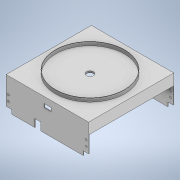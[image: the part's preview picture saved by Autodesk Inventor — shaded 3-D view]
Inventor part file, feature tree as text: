
AUTODESK INVENTOR PART (.ipt)
format: ipt  version: 2022 (Build 260153000, 153)  size: 213,504 bytes
history: native  units: in
note: dims shown in document units (in); Inventor stores cm internally (conversion verified against a paired STEP export)
features: extrude x9, sketch x6
ambient origin geometry x8: Origin, YZ Plane, XZ Plane, XY Plane, X Axis, Y Axis, Z Axis, Center Point
bodies: Solid1 (feature_tree)
feature tree (15):
  sketch  "Sketch2"  dims[d0=4.685in d1=1.5748in]
  sketch  "Sketch3"  dims[d2=0.315in d3=0.9449in]
  extrude  "Extrusion1"  Depth=1.5748in
  extrude  "Extrusion2"  Depth=0.315in
  extrude  "Extrusion3"  Depth=0.3031in
  sketch  "Sketch4"  dims[d4=0.1102in d5=0.3031in]
  extrude  "Extrusion4"  Depth=0.1102in
  extrude  "Extrusion5"  Depth=0.315in
  extrude  "Extrusion6"  Depth=0.6998in
  extrude  "Extrusion7"  Depth=0.6998in
  extrude  "Extrusion8"  Depth=0.6998in
  extrude  "Extrusion9"  Depth=0.6998in
  sketch  "Sketch5"  dims[d6=0.2053in d7=0.1102in]
  sketch  "Sketch6"  dims[d8=0.3346in d9=0.315in]
  sketch  "Sketch7"  dims[d10=0.9449in d12=0.1102in d13=0.3031in d15=0.1929in d16=0.1102in d17=0.3346in d18=0.4055in d19=0.1969in d20=1.0236in d21=4.6457in d22=4.8031in d23=4.7244in d24=4.8819in d25=0.7874in d26=0.0in d27=6.6373in d28=0.0in d29=0.1508in d30=1.0748in d31=0.0in d32=0.0in d33=3.937in d34=3.9764in d35=0.3937in d36=0.3937in d37=0.0in d38=0.1969in d39=0.0in d40=0.3543in d41=0.4488in d42=0.1969in d43=0.0in d44=3.937in d45=39.3701in d46=0.0in d47=0.0in d53=1.0236in d54=0.0in d55=1.5748in d56=0.315in d57=1.5748in d58=0.315in d59=5.1624in d60=0.0in d61=0.6998in d62=0.0in]
